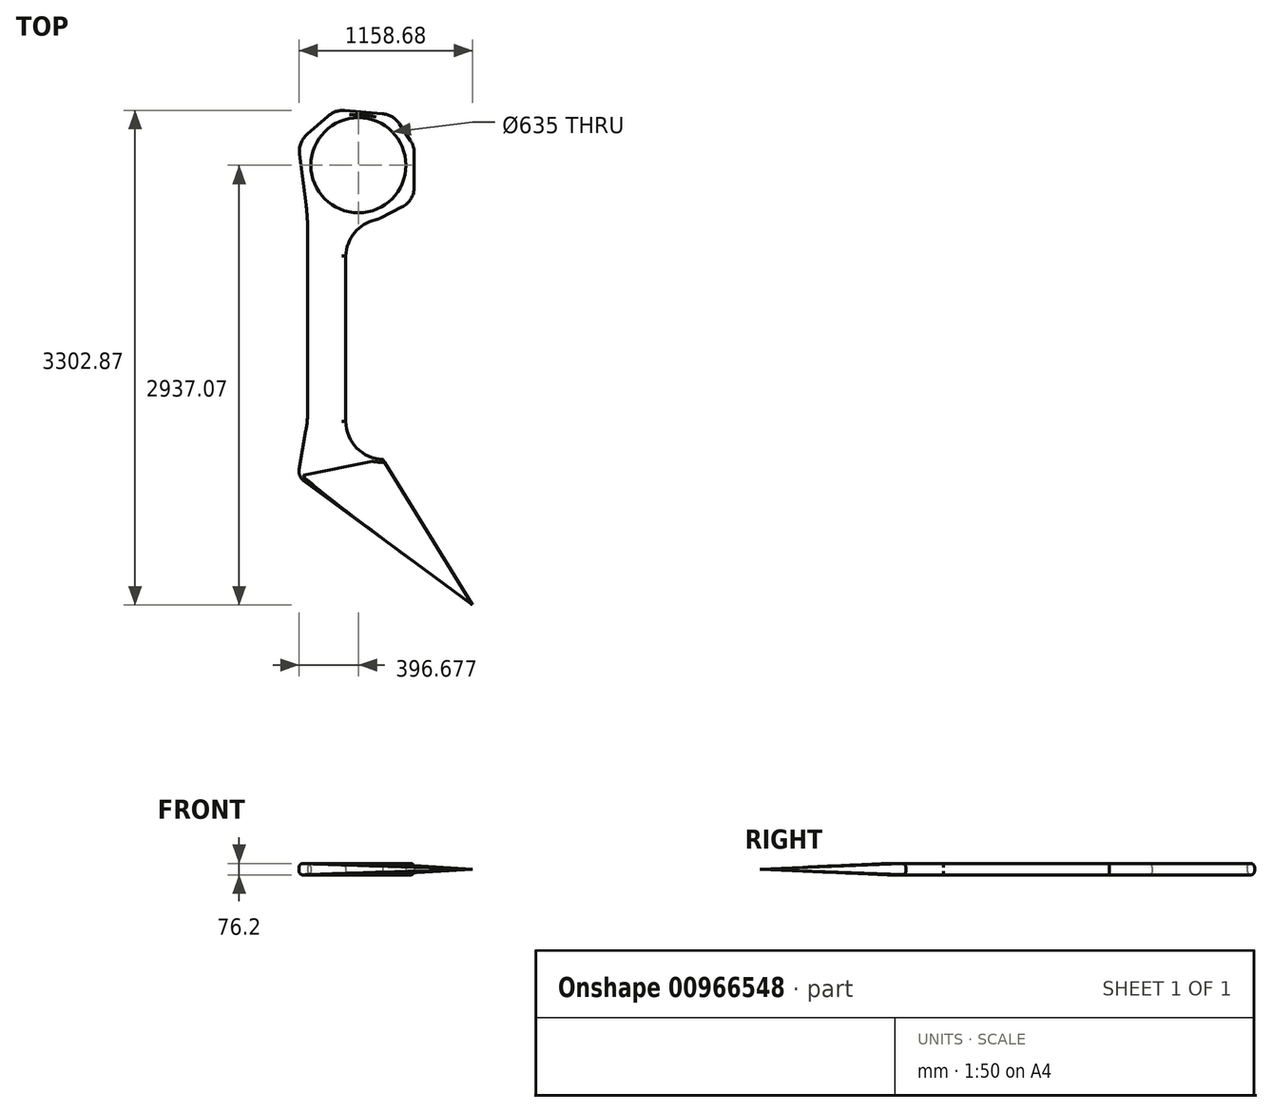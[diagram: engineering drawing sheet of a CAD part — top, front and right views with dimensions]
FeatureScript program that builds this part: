
annotation { "Feature Type Name" : "Feature", "Feature Type Description" : "" }
export const myFeature = defineFeature(function(context is Context, id is Id, definition is map)
    precondition{}
    {
        {
            var Q0;
            Q0=qCreatedBy(makeId("Top.planeOp"),FACE);
            var sketch = newSketch(context, id + "F0", { "sketchPlane" : qUnion([Q0])});
            skArc(sketch, "E0", {"start": v(-2204.79, -444.73) * mm, "mid": v(-2132.37, -621.02) * mm, "end": v(-1957.73, -697.32) * mm});
            skArc(sketch, "E1", {"start": v(-1989.5, 905.52) * mm, "mid": v(-2141.61, 822.2) * mm, "end": v(-2204.79, 660.67) * mm});
            skLineSegment(sketch, "E2", {"start": v(-2204.79, -444.73) * mm, "end": v(-2204.79, 660.67) * mm});
            skCircle(sketch, "E3", {"center": v(-2120.58, 1266.37) * mm, "radius": 317.5 * mm});
            skLineSegment(sketch, "E4", {"start": v(-1957.73, -697.32) * mm, "end": v(-1358.58, -1670.7) * mm});
            skLineSegment(sketch, "E5", {"start": v(-1358.58, -1670.7) * mm, "end": v(-2524.11, -811.83) * mm});
            skLineSegment(sketch, "E6", {"start": v(-2458.79, -431.15) * mm, "end": v(-2458.79, 905.52) * mm});
            skLineSegment(sketch, "E7", {"start": v(-2167.84, -575.35) * mm, "end": v(-2167.84, -575.35) * mm});
            skPoint(sketch, "E7.second.point", {"position": v(-2167.84, -575.35) * mm});
            skLineSegment(sketch, "E8", {"start": v(-2524.11, -811.83) * mm, "end": v(-1957.73, -697.32) * mm});
            skLineSegment(sketch, "E9", {"start": v(-2300.1, -762.7) * mm, "end": v(-1358.58, -1670.7) * mm});
            skLineSegment(sketch, "E10", {"start": v(-2458.79, -431.15) * mm, "end": v(-2524.11, -811.83) * mm});
            skLineSegment(sketch, "E11", {"start": v(-2458.79, 905.52) * mm, "end": v(-2524.11, 1419.55) * mm});
            skLineSegment(sketch, "E12", {"start": v(-2524.11, 1419.55) * mm, "end": v(-2275.61, 1636.98) * mm});
            skLineSegment(sketch, "E13", {"start": v(-1887.76, 1604.84) * mm, "end": v(-1747.51, 1393.07) * mm});
            skLineSegment(sketch, "E14", {"start": v(-2275.61, 1636.98) * mm, "end": v(-1887.76, 1604.84) * mm});
            skLineSegment(sketch, "E15", {"start": v(-1747.51, 1393.07) * mm, "end": v(-1747.51, 1029.05) * mm});
            skLineSegment(sketch, "E16", {"start": v(-1747.51, 1029.05) * mm, "end": v(-1989.5, 905.52) * mm});
            skSolve(sketch);
        }
        {
            var Q0;
            {var subQ2=sQuery(id+"F0.wireOp",EDGE,"E0");Q0=makeQuery(id+"F0.imprint","IMPRINT",FACE,{"disambiguationData":[TD([[makeQuery(id+"F0.imprint","IMPRINT",EDGE,{"derivedFrom":subQ2}),-1.0]])]});}
            extrude(context, id + "F1", {"entities" : qUnion([Q0]), "endBound" : BoundingType.SYMMETRIC, "depth" : 76.2 * mm, "offsetDistance" : 25.4 * mm});
        }
        {
            var Q0;
            Q0=makeQuery(id+"F1.opExtrude","SWEPT_EDGE",EDGE,{"disambiguationData":[OSD([sQuery(id+"F0.wireOp",EDGE,"E1"),sQuery(id+"F0.wireOp",EDGE,"E16")])]});
            fillet(context, id + "F2", {"entities" : qUnion([Q0]), "radius" : 152.4 * mm, "tangentPropagation" : true, "allowEdgeOverflow" : false});
        }
        {
            var Q0;
            Q0=makeQuery(id+"F1.opExtrude","SWEPT_EDGE",EDGE,{"disambiguationData":[OSD([sQuery(id+"F0.wireOp",EDGE,"E15"),sQuery(id+"F0.wireOp",EDGE,"E16")])]});
            var Q1;
            Q1=makeQuery(id+"F1.opExtrude","SWEPT_EDGE",EDGE,{"disambiguationData":[OSD([sQuery(id+"F0.wireOp",EDGE,"E13"),sQuery(id+"F0.wireOp",EDGE,"E15")])]});
            var Q2;
            Q2=makeQuery(id+"F1.opExtrude","SWEPT_EDGE",EDGE,{"disambiguationData":[OSD([sQuery(id+"F0.wireOp",EDGE,"E13"),sQuery(id+"F0.wireOp",EDGE,"E14")])]});
            var Q3;
            Q3=makeQuery(id+"F1.opExtrude","SWEPT_EDGE",EDGE,{"disambiguationData":[OSD([sQuery(id+"F0.wireOp",EDGE,"E12"),sQuery(id+"F0.wireOp",EDGE,"E14")])]});
            var Q4;
            Q4=makeQuery(id+"F1.opExtrude","SWEPT_EDGE",EDGE,{"disambiguationData":[OSD([sQuery(id+"F0.wireOp",EDGE,"E11"),sQuery(id+"F0.wireOp",EDGE,"E12")])]});
            fillet(context, id + "F3", {"entities" : qUnion([Q0, Q1, Q2, Q3, Q4]), "radius" : 152.4 * mm, "tangentPropagation" : true, "allowEdgeOverflow" : false});
        }
        {
            var Q0;
            Q0=makeQuery(id+"F1.opExtrude","SWEPT_EDGE",EDGE,{"disambiguationData":[OSD([sQuery(id+"F0.wireOp",EDGE,"E6"),sQuery(id+"F0.wireOp",EDGE,"E10")])]});
            fillet(context, id + "F4", {"entities" : qUnion([Q0]), "radius" : 889 * mm, "tangentPropagation" : true, "allowEdgeOverflow" : false});
        }
        {
            var Q0;
            Q0=makeQuery(id+"F1.opExtrude","SWEPT_EDGE",EDGE,{"disambiguationData":[OSD([sQuery(id+"F0.wireOp",EDGE,"E6"),sQuery(id+"F0.wireOp",EDGE,"E11")])]});
            fillet(context, id + "F5", {"entities" : qUnion([Q0]), "radius" : 1524 * mm, "tangentPropagation" : true, "allowEdgeOverflow" : false});
        }
        {
            var Q1;
            Q1=sQuery(id+"F0.wireOp",VERTEX,"E4.end");
            var Q2;
            Q2=makeQuery(id+"F1.opExtrude","SWEPT_FACE",FACE,{"disambiguationData":[OSD([sQuery(id+"F0.wireOp",EDGE,"E8")])]});
            loft(context, id + "F6", {"operationType" : NewBodyOperationType.ADD, "sheetProfilesArray" : [{ "sheetProfileEntities" : qUnion([Q1]) }, { "sheetProfileEntities" : qUnion([Q2]) }]});
        }
        {
            var Q0;
            {var subQ0=sQuery(id+"F0.wireOp",EDGE,"E10");var subQ1=sQuery(id+"F0.wireOp",EDGE,"E8");var subQ2=sQuery(id+"F0.wireOp",EDGE,"E5");Q0=makeQuery(id+"F6.boolean.opBoolean","MERGE",EDGE,{"derivedFrom":[makeQuery(id+"F1.opExtrude","SWEPT_EDGE",EDGE,{"disambiguationData":[OSD([subQ2,subQ1,subQ0])]}),makeQuery(id+"F6.opLoft","MID_CAP_EDGE",EDGE,{"disambiguationData":[OSD([subQ2,subQ1,subQ0])],"capPos":1.0})]});}
            fillet(context, id + "F7", {"entities" : qUnion([Q0]), "radius" : 76.2 * mm, "tangentPropagation" : true, "allowEdgeOverflow" : false});
        }
        {
            var Q0;
            Q0=makeQuery(id+"F1.opExtrude","CAP_EDGE",EDGE,{"disambiguationData":[OSD([sQuery(id+"F0.wireOp",EDGE,"E2")])],"isStart":false});
            var Q1;
            Q1=makeQuery(id+"F1.opExtrude","CAP_EDGE",EDGE,{"disambiguationData":[OSD([sQuery(id+"F0.wireOp",EDGE,"E16")])],"isStart":false});
            var Q2;
            Q2=makeQuery(id+"F1.opExtrude","CAP_EDGE",EDGE,{"disambiguationData":[OSD([sQuery(id+"F0.wireOp",EDGE,"E16")])],"isStart":true});
            var Q3;
            Q3=makeQuery(id+"F1.opExtrude","CAP_EDGE",EDGE,{"disambiguationData":[OSD([sQuery(id+"F0.wireOp",EDGE,"E2")])],"isStart":true});
            var Q4;
            Q4=makeQuery(id+"F1.opExtrude","CAP_EDGE",EDGE,{"disambiguationData":[OSD([sQuery(id+"F0.wireOp",EDGE,"E3")])],"isStart":false});
            var Q5;
            Q5=makeQuery(id+"F1.opExtrude","CAP_EDGE",EDGE,{"disambiguationData":[OSD([sQuery(id+"F0.wireOp",EDGE,"E3")])],"isStart":true});
            fillet(context, id + "F8", {"entities" : qUnion([Q0, Q1, Q2, Q3, Q4, Q5]), "radius" : 25.4 * mm, "tangentPropagation" : true, "allowEdgeOverflow" : false});
        }
    });
